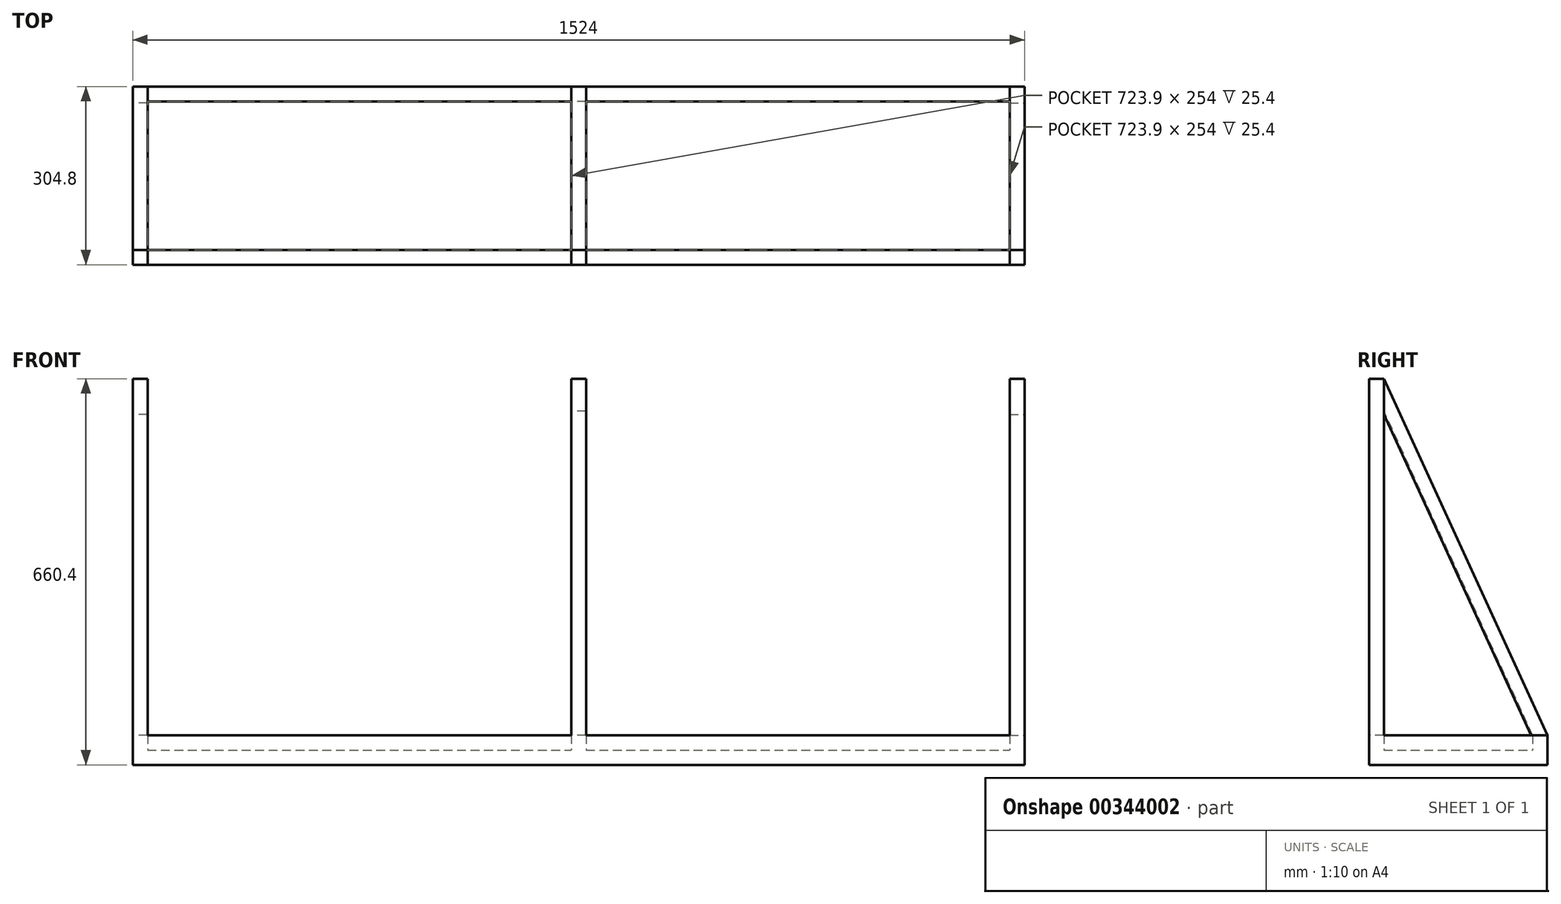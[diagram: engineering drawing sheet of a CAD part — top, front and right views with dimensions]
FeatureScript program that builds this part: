
annotation { "Feature Type Name" : "Feature", "Feature Type Description" : "" }
export const myFeature = defineFeature(function(context is Context, id is Id, definition is map)
    precondition{}
    {
        {
            var Q0;
            Q0=qCreatedBy(makeId("Top.planeOp"),FACE);
            var sketch = newSketch(context, id + "F0", { "sketchPlane" : qUnion([Q0])});
            skLineSegment(sketch, "E0.bottom", {"start": v(0, 304.8) * mm, "end": v(1524, 304.8) * mm});
            skLineSegment(sketch, "E0.top", {"start": v(0, 0) * mm, "end": v(1524, 0) * mm});
            skLineSegment(sketch, "E0.left", {"start": v(0, 304.8) * mm, "end": v(0, 0) * mm});
            skLineSegment(sketch, "E0.right", {"start": v(1524, 304.8) * mm, "end": v(1524, 0) * mm});
            skSolve(sketch);
        }
        {
            var Q0;
            Q0 = qSketchRegion(id + "F0", true);
            extrude(context, id + "F1", {"entities" : qUnion([Q0]), "depth" : 25.4 * mm});
        }
        {
            var Q0;
            Q0=makeQuery(id+"F1.opExtrude","CAP_FACE",FACE,{"disambiguationData":[OSD([sQuery(id+"F0.wireOp",EDGE,"E0.bottom"),sQuery(id+"F0.wireOp",EDGE,"E0.top"),sQuery(id+"F0.wireOp",EDGE,"E0.left"),sQuery(id+"F0.wireOp",EDGE,"E0.right")])],"isStart":false});
            var sketch = newSketch(context, id + "F2", { "sketchPlane" : qUnion([Q0])});
            skLineSegment(sketch, "E1.bottom", {"start": v(0, 0) * mm, "end": v(1524, 0) * mm});
            skLineSegment(sketch, "E1.top", {"start": v(0, 304.8) * mm, "end": v(1524, 304.8) * mm});
            skLineSegment(sketch, "E1.left", {"start": v(0, 0) * mm, "end": v(0, 304.8) * mm});
            skLineSegment(sketch, "E1.right", {"start": v(1524, 0) * mm, "end": v(1524, 304.8) * mm});
            skLineSegment(sketch, "E2.bottom", {"start": v(25.4, 25.4) * mm, "end": v(749.3, 25.4) * mm});
            skLineSegment(sketch, "E2.top", {"start": v(25.4, 279.4) * mm, "end": v(749.3, 279.4) * mm});
            skLineSegment(sketch, "E2.left", {"start": v(25.4, 25.4) * mm, "end": v(25.4, 279.4) * mm});
            skLineSegment(sketch, "E2.right", {"start": v(1498.6, 25.4) * mm, "end": v(1498.6, 279.4) * mm});
            skLineSegment(sketch, "E3", {"start": v(749.3, 279.4) * mm, "end": v(749.3, 25.4) * mm});
            skLineSegment(sketch, "E4", {"start": v(774.7, 279.4) * mm, "end": v(774.7, 25.4) * mm});
            skLineSegment(sketch, "E5.trimOffspring", {"start": v(774.7, 279.4) * mm, "end": v(1498.6, 279.4) * mm});
            skLineSegment(sketch, "E6.trimOffspring", {"start": v(774.7, 25.4) * mm, "end": v(1498.6, 25.4) * mm});
            skSolve(sketch);
        }
        {
            var Q0;
            Q0 = qSketchRegion(id + "F2", true);
            extrude(context, id + "F3", {"entities" : qUnion([Q0]), "operationType" : NewBodyOperationType.ADD, "depth" : 25.4 * mm});
        }
        {
            var Q0;
            Q0=makeQuery(id+"F3.opExtrude","CAP_FACE",FACE,{"disambiguationData":[OSD([sQuery(id+"F2.wireOp",EDGE,"E1.bottom"),sQuery(id+"F2.wireOp",EDGE,"E1.top"),sQuery(id+"F2.wireOp",EDGE,"E1.left"),sQuery(id+"F2.wireOp",EDGE,"E1.right"),sQuery(id+"F2.wireOp",EDGE,"E2.bottom"),sQuery(id+"F2.wireOp",EDGE,"E2.top"),sQuery(id+"F2.wireOp",EDGE,"E2.left"),sQuery(id+"F2.wireOp",EDGE,"E2.right"),sQuery(id+"F2.wireOp",EDGE,"E3"),sQuery(id+"F2.wireOp",EDGE,"E4"),sQuery(id+"F2.wireOp",EDGE,"E5.trimOffspring"),sQuery(id+"F2.wireOp",EDGE,"E6.trimOffspring")])],"isStart":false});
            var sketch = newSketch(context, id + "F4", { "sketchPlane" : qUnion([Q0])});
            skLineSegment(sketch, "E7.bottom", {"start": v(0, 0) * mm, "end": v(25.4, 0) * mm});
            skLineSegment(sketch, "E7.top", {"start": v(0, 25.4) * mm, "end": v(25.4, 25.4) * mm});
            skLineSegment(sketch, "E7.left", {"start": v(0, 0) * mm, "end": v(0, 25.4) * mm});
            skLineSegment(sketch, "E7.right", {"start": v(25.4, 0) * mm, "end": v(25.4, 25.4) * mm});
            skLineSegment(sketch, "E8.bottom", {"start": v(749.3, 25.4) * mm, "end": v(774.7, 25.4) * mm});
            skLineSegment(sketch, "E8.top", {"start": v(749.3, 0) * mm, "end": v(774.7, 0) * mm});
            skLineSegment(sketch, "E8.left", {"start": v(749.3, 25.4) * mm, "end": v(749.3, 0) * mm});
            skLineSegment(sketch, "E8.right", {"start": v(774.7, 25.4) * mm, "end": v(774.7, 0) * mm});
            skLineSegment(sketch, "E9.bottom", {"start": v(1498.6, 25.4) * mm, "end": v(1524, 25.4) * mm});
            skLineSegment(sketch, "E9.top", {"start": v(1498.6, 0) * mm, "end": v(1524, 0) * mm});
            skLineSegment(sketch, "E9.left", {"start": v(1498.6, 25.4) * mm, "end": v(1498.6, 0) * mm});
            skLineSegment(sketch, "E9.right", {"start": v(1524, 25.4) * mm, "end": v(1524, 0) * mm});
            skSolve(sketch);
        }
        {
            var Q0;
            Q0 = qSketchRegion(id + "F4", true);
            extrude(context, id + "F5", {"entities" : qUnion([Q0]), "operationType" : NewBodyOperationType.ADD, "depth" : 609.6 * mm});
        }
        {
            var Q0;
            Q0=makeQuery(id+"F5.boolean.opBoolean","MERGE",FACE,{"derivedFrom":[makeQuery(id+"F3.boolean.opBoolean","MERGE",FACE,{"derivedFrom":[makeQuery(id+"F1.opExtrude","SWEPT_FACE",FACE,{"disambiguationData":[OSD([sQuery(id+"F0.wireOp",EDGE,"E0.left")])]}),makeQuery(id+"F3.opExtrude","SWEPT_FACE",FACE,{"disambiguationData":[OSD([sQuery(id+"F2.wireOp",EDGE,"E1.left")])]})]}),makeQuery(id+"F5.opExtrude","SWEPT_FACE",FACE,{"disambiguationData":[OSD([sQuery(id+"F4.wireOp",EDGE,"E7.left")])]})]});
            var sketch = newSketch(context, id + "F6", { "sketchPlane" : qUnion([Q0])});
            skLineSegment(sketch, "E10", {"start": v(-25.4, 660.4) * mm, "end": v(-25.4, 599.44) * mm});
            skLineSegment(sketch, "E11", {"start": v(-25.4, 599.44) * mm, "end": v(-276.86, 50.8) * mm});
            skLineSegment(sketch, "E12", {"start": v(-276.86, 50.8) * mm, "end": v(-304.8, 50.8) * mm});
            skLineSegment(sketch, "E13", {"start": v(-304.8, 50.8) * mm, "end": v(-25.4, 660.4) * mm});
            skSolve(sketch);
        }
        {
            var Q0;
            Q0 = qSketchRegion(id + "F6", true);
            extrude(context, id + "F7", {"entities" : qUnion([Q0]), "oppositeDirection" : true, "depth" : 25.4 * mm});
        }
        {
            var Q0;
            Q0=makeQuery(id+"F5.opExtrude","SWEPT_FACE",FACE,{"disambiguationData":[OSD([sQuery(id+"F4.wireOp",EDGE,"E8.left")])]});
            var sketch = newSketch(context, id + "F8", { "sketchPlane" : qUnion([Q0])});
            skLineSegment(sketch, "E14", {"start": v(-25.4, 660.4) * mm, "end": v(-304.8, 50.8) * mm});
            skLineSegment(sketch, "E15", {"start": v(-304.8, 50.8) * mm, "end": v(-279.4, 50.8) * mm});
            skLineSegment(sketch, "E16", {"start": v(-279.4, 50.8) * mm, "end": v(-25.4, 604.98) * mm});
            skLineSegment(sketch, "E17", {"start": v(-25.4, 604.98) * mm, "end": v(-25.4, 660.4) * mm});
            skSolve(sketch);
        }
        {
            var Q0;
            Q0 = qSketchRegion(id + "F8", true);
            extrude(context, id + "F9", {"entities" : qUnion([Q0]), "operationType" : NewBodyOperationType.ADD, "oppositeDirection" : true, "depth" : 25.4 * mm});
        }
        {
            var Q0;
            Q0=makeQuery(id+"F5.boolean.opBoolean","MERGE",FACE,{"derivedFrom":[makeQuery(id+"F3.boolean.opBoolean","MERGE",FACE,{"derivedFrom":[makeQuery(id+"F1.opExtrude","SWEPT_FACE",FACE,{"disambiguationData":[OSD([sQuery(id+"F0.wireOp",EDGE,"E0.right")])]}),makeQuery(id+"F3.opExtrude","SWEPT_FACE",FACE,{"disambiguationData":[OSD([sQuery(id+"F2.wireOp",EDGE,"E1.right")])]})]}),makeQuery(id+"F5.opExtrude","SWEPT_FACE",FACE,{"disambiguationData":[OSD([sQuery(id+"F4.wireOp",EDGE,"E9.right")])]})]});
            var sketch = newSketch(context, id + "F10", { "sketchPlane" : qUnion([Q0])});
            skLineSegment(sketch, "E18", {"start": v(304.8, 50.8) * mm, "end": v(25.4, 660.4) * mm});
            skLineSegment(sketch, "E19", {"start": v(25.4, 660.4) * mm, "end": v(25.4, 599.44) * mm});
            skLineSegment(sketch, "E20", {"start": v(25.4, 599.44) * mm, "end": v(276.86, 50.8) * mm});
            skLineSegment(sketch, "E21", {"start": v(276.86, 50.8) * mm, "end": v(304.8, 50.8) * mm});
            skSolve(sketch);
        }
        {
            var Q0;
            Q0 = qSketchRegion(id + "F10", true);
            extrude(context, id + "F11", {"entities" : qUnion([Q0]), "oppositeDirection" : true, "depth" : 25.4 * mm});
        }
    });
